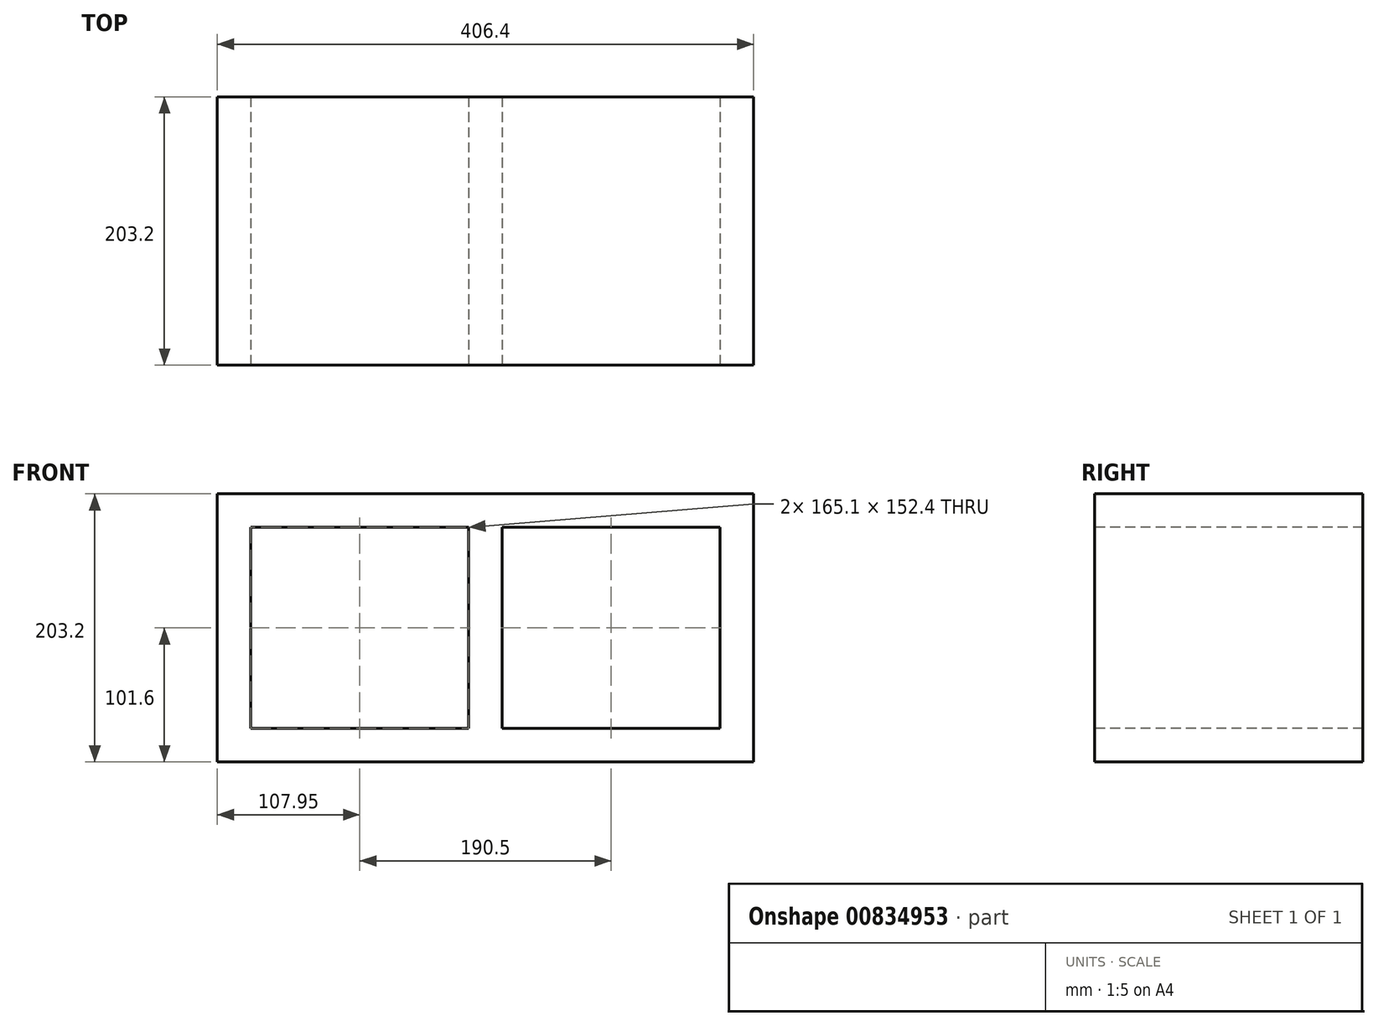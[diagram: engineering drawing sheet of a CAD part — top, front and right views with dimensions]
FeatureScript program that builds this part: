
annotation { "Feature Type Name" : "Feature", "Feature Type Description" : "" }
export const myFeature = defineFeature(function(context is Context, id is Id, definition is map)
    precondition{}
    {
        {
            var Q0;
            Q0=qCreatedBy(makeId("Top.planeOp"),FACE);
            var sketch = newSketch(context, id + "F0", { "sketchPlane" : qUnion([Q0])});
            skLineSegment(sketch, "E0.bottom", {"start": v(0, 0) * mm, "end": v(406.4, 0) * mm});
            skLineSegment(sketch, "E0.top", {"start": v(0, 203.2) * mm, "end": v(406.4, 203.2) * mm});
            skLineSegment(sketch, "E0.left", {"start": v(0, 0) * mm, "end": v(0, 203.2) * mm});
            skLineSegment(sketch, "E0.right", {"start": v(406.4, 0) * mm, "end": v(406.4, 203.2) * mm});
            skSolve(sketch);
        }
        {
            var Q0;
            Q0 = qSketchRegion(id + "F0", true);
            extrude(context, id + "F1", {"entities" : qUnion([Q0]), "depth" : 203.2 * mm, "offsetDistance" : 25.4 * mm});
        }
        {
            var Q0;
            Q0=makeQuery(id+"F1.opExtrude","SWEPT_FACE",FACE,{"disambiguationData":[OSD([sQuery(id+"F0.wireOp",EDGE,"E0.bottom")])]});
            var sketch = newSketch(context, id + "F2", { "sketchPlane" : qUnion([Q0])});
            skLineSegment(sketch, "E1.bottom", {"start": v(25.4, 177.8) * mm, "end": v(190.5, 177.8) * mm});
            skLineSegment(sketch, "E1.top", {"start": v(25.4, 25.4) * mm, "end": v(190.5, 25.4) * mm});
            skLineSegment(sketch, "E1.left", {"start": v(25.4, 177.8) * mm, "end": v(25.4, 25.4) * mm});
            skLineSegment(sketch, "E1.right", {"start": v(190.5, 177.8) * mm, "end": v(190.5, 25.4) * mm});
            skLineSegment(sketch, "E2", {"start": v(203.2, 203.2) * mm, "end": v(203.2, 0) * mm, "construction": true});
            skLineSegment(sketch, "E3", {"start": v(203.2, 101.6) * mm, "end": v(0, 101.6) * mm, "construction": true});
            skLineSegment(sketch, "E4.MirrorCS", {"start": v(215.9, 177.8) * mm, "end": v(215.9, 25.4) * mm});
            skLineSegment(sketch, "E5.MirrorCS", {"start": v(381, 177.8) * mm, "end": v(215.9, 177.8) * mm});
            skLineSegment(sketch, "E6.MirrorCS", {"start": v(381, 177.8) * mm, "end": v(381, 25.4) * mm});
            skLineSegment(sketch, "E7.MirrorCS", {"start": v(381, 25.4) * mm, "end": v(215.9, 25.4) * mm});
            skSolve(sketch);
        }
        {
            var Q0;
            Q0 = qSketchRegion(id + "F2", true);
            extrude(context, id + "F3", {"entities" : qUnion([Q0]), "operationType" : NewBodyOperationType.REMOVE, "endBound" : BoundingType.THROUGH_ALL, "oppositeDirection" : true, "depth" : 25.4 * mm, "offsetDistance" : 25.4 * mm});
        }
        {
            var Q0;
            Q0 = qSketchRegion(id + "F2", true);
            extrude(context, id + "F4", {"entities" : qUnion([Q0]), "operationType" : NewBodyOperationType.REMOVE, "endBound" : BoundingType.THROUGH_ALL, "oppositeDirection" : true, "depth" : 25.4 * mm, "offsetDistance" : 25.4 * mm});
        }
    });
